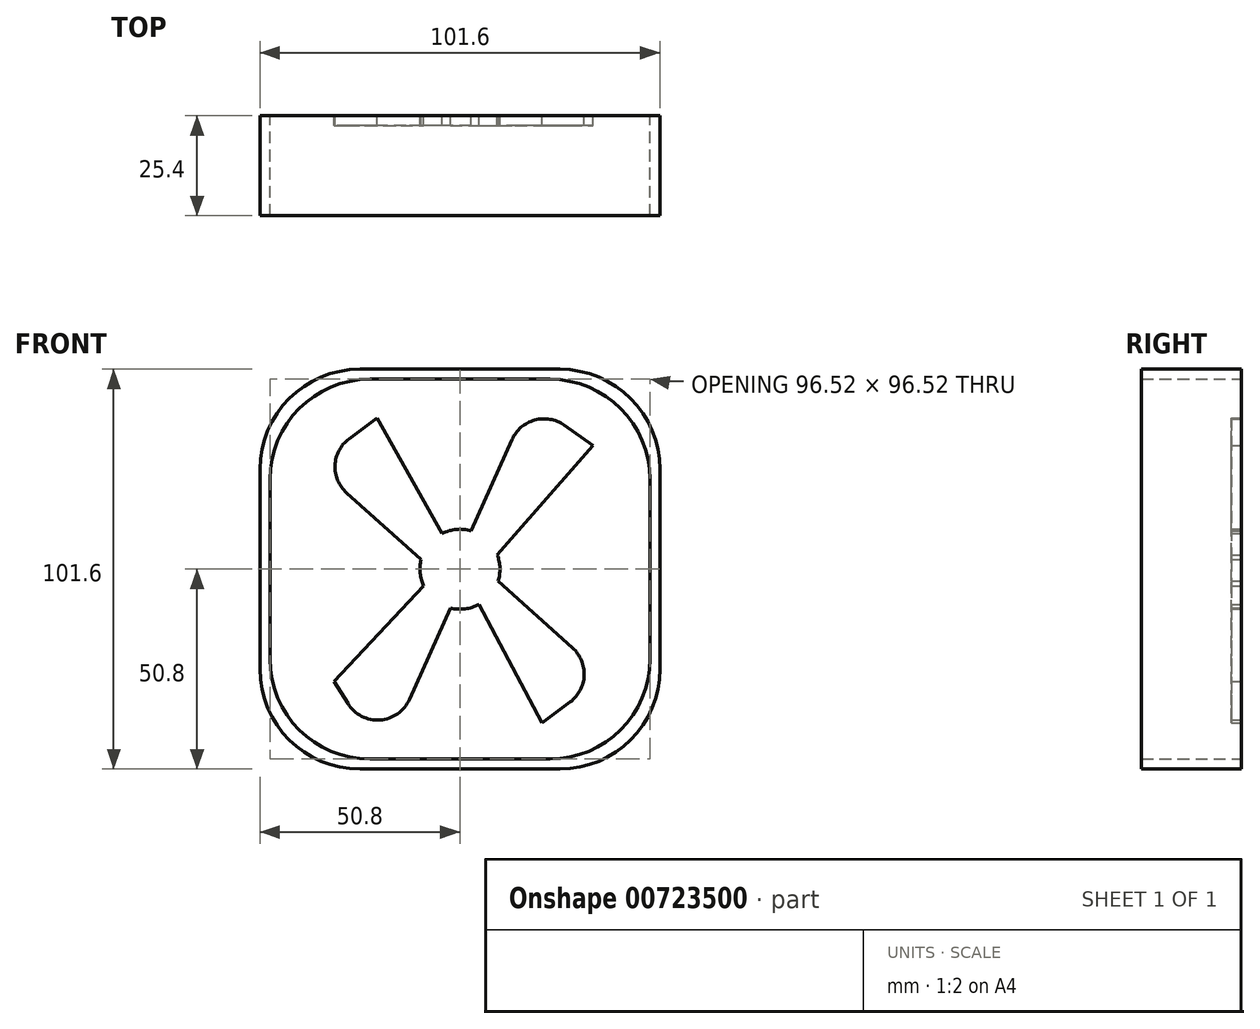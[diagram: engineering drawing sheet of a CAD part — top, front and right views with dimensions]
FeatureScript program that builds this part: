
annotation { "Feature Type Name" : "Feature", "Feature Type Description" : "" }
export const myFeature = defineFeature(function(context is Context, id is Id, definition is map)
    precondition{}
    {
        {
            var Q0;
            Q0=qCreatedBy(makeId("Front.planeOp"),FACE);
            var sketch = newSketch(context, id + "F0", { "sketchPlane" : qUnion([Q0])});
            skLineSegment(sketch, "E0.bottom", {"start": v(25.4, 50.8) * mm, "end": v(-25.4, 50.8) * mm});
            skLineSegment(sketch, "E0.top", {"start": v(25.4, -50.8) * mm, "end": v(-25.4, -50.8) * mm});
            skLineSegment(sketch, "E0.left", {"start": v(50.8, 25.4) * mm, "end": v(50.8, -25.4) * mm});
            skLineSegment(sketch, "E0.right", {"start": v(-50.8, 25.4) * mm, "end": v(-50.8, -25.4) * mm});
            skPoint(sketch, "E0.middle", {"position": v(0, 0) * mm});
            skPoint(sketch, "E1.visualSharp", {"position": v(-50.8, 50.8) * mm});
            skArc(sketch, "E1.filletArc", {"start": v(-25.4, 50.8) * mm, "mid": v(-43.36, 43.36) * mm, "end": v(-50.8, 25.4) * mm});
            skPoint(sketch, "E2.visualSharp", {"position": v(50.8, 50.8) * mm});
            skArc(sketch, "E2.filletArc", {"start": v(50.8, 25.4) * mm, "mid": v(43.36, 43.36) * mm, "end": v(25.4, 50.8) * mm});
            skPoint(sketch, "E3.visualSharp", {"position": v(50.8, -50.8) * mm});
            skArc(sketch, "E3.filletArc", {"start": v(25.4, -50.8) * mm, "mid": v(43.36, -43.36) * mm, "end": v(50.8, -25.4) * mm});
            skPoint(sketch, "E4.visualSharp", {"position": v(-50.8, -50.8) * mm});
            skArc(sketch, "E4.filletArc", {"start": v(-50.8, -25.4) * mm, "mid": v(-43.36, -43.36) * mm, "end": v(-25.4, -50.8) * mm});
            skLineSegment(sketch, "E5.bottom", {"start": v(-22.86, 48.26) * mm, "end": v(22.86, 48.26) * mm});
            skLineSegment(sketch, "E5.top", {"start": v(-22.86, -48.26) * mm, "end": v(22.86, -48.26) * mm});
            skLineSegment(sketch, "E5.left", {"start": v(-48.26, 22.86) * mm, "end": v(-48.26, -22.86) * mm});
            skLineSegment(sketch, "E5.right", {"start": v(48.26, 22.86) * mm, "end": v(48.26, -22.86) * mm});
            skPoint(sketch, "E6.visualSharp", {"position": v(-48.26, 48.26) * mm});
            skArc(sketch, "E6.filletArc", {"start": v(-22.86, 48.26) * mm, "mid": v(-40.82, 40.82) * mm, "end": v(-48.26, 22.86) * mm});
            skPoint(sketch, "E7.visualSharp", {"position": v(48.26, 48.26) * mm});
            skArc(sketch, "E7.filletArc", {"start": v(48.26, 22.86) * mm, "mid": v(40.82, 40.82) * mm, "end": v(22.86, 48.26) * mm});
            skPoint(sketch, "E8.visualSharp", {"position": v(48.26, -48.26) * mm});
            skArc(sketch, "E8.filletArc", {"start": v(22.86, -48.26) * mm, "mid": v(40.82, -40.82) * mm, "end": v(48.26, -22.86) * mm});
            skPoint(sketch, "E9.visualSharp", {"position": v(-48.26, -48.26) * mm});
            skArc(sketch, "E9.filletArc", {"start": v(-48.26, -22.86) * mm, "mid": v(-40.82, -40.82) * mm, "end": v(-22.86, -48.26) * mm});
            skSolve(sketch);
        }
        {
            var Q0;
            Q0=makeQuery(id+"F0.imprint","IMPRINT",FACE,{"disambiguationData":[TD([[makeQuery(id+"F0.imprint","IMPRINT",EDGE,{"derivedFrom":sQuery(id+"F0.wireOp",EDGE,"E0.bottom")}),1.0]])]});
            extrude(context, id + "F1", {"entities" : qUnion([Q0]), "depth" : 25.4 * mm, "offsetDistance" : 25.4 * mm});
        }
        {
            var Q0;
            Q0=qCreatedBy(makeId("Front.planeOp"),FACE);
            var sketch = newSketch(context, id + "F2", { "sketchPlane" : qUnion([Q0])});
            skCircle(sketch, "E10", {"center": v(0, 0) * mm, "radius": 10.16 * mm});
            skLineSegment(sketch, "E11", {"start": v(2.86, 9.75) * mm, "end": v(13.22, 32.94) * mm});
            skLineSegment(sketch, "E12", {"start": v(9.48, 3.66) * mm, "end": v(33.76, 31.45) * mm});
            skLineSegment(sketch, "E13", {"start": v(33.76, 31.45) * mm, "end": v(26.47, 36.59) * mm});
            skArc(sketch, "E14.filletArc", {"start": v(26.47, 36.59) * mm, "mid": v(18.99, 37.9) * mm, "end": v(13.22, 32.94) * mm});
            skLineSegment(sketch, "E15", {"start": v(-4.53, 9.1) * mm, "end": v(-21.09, 38.48) * mm});
            skLineSegment(sketch, "E16", {"start": v(-21.09, 38.48) * mm, "end": v(-28.2, 33.1) * mm});
            skArc(sketch, "E17.filletArc", {"start": v(-28.2, 33.1) * mm, "mid": v(-31.73, 26.38) * mm, "end": v(-28.78, 19.38) * mm});
            skLineSegment(sketch, "E18", {"start": v(-28.78, 19.38) * mm, "end": v(-9.87, 2.42) * mm});
            skLineSegment(sketch, "E19", {"start": v(-2.44, -9.86) * mm, "end": v(-12.8, -33.05) * mm});
            skLineSegment(sketch, "E20", {"start": v(-8.87, -3.97) * mm, "end": v(-31.98, -28.54) * mm});
            skLineSegment(sketch, "E21", {"start": v(-31.98, -28.54) * mm, "end": v(-28.46, -34.15) * mm});
            skArc(sketch, "E22.filletArc", {"start": v(-28.46, -34.15) * mm, "mid": v(-20.3, -38.3) * mm, "end": v(-12.8, -33.05) * mm});
            skLineSegment(sketch, "E23", {"start": v(4.84, -8.93) * mm, "end": v(20.91, -39.1) * mm});
            skLineSegment(sketch, "E24", {"start": v(20.91, -39.1) * mm, "end": v(28.02, -33.74) * mm});
            skArc(sketch, "E25.filletArc", {"start": v(28.02, -33.74) * mm, "mid": v(31.56, -27) * mm, "end": v(28.6, -20) * mm});
            skLineSegment(sketch, "E26", {"start": v(28.6, -20) * mm, "end": v(9.7, -3.05) * mm});
            skSolve(sketch);
        }
        {
            var Q0;
            Q0 = qSketchRegion(id + "F2", true);
            extrude(context, id + "F3", {"entities" : qUnion([Q0]), "depth" : 2.54 * mm, "offsetDistance" : 25.4 * mm});
        }
    });
